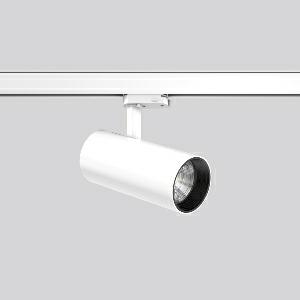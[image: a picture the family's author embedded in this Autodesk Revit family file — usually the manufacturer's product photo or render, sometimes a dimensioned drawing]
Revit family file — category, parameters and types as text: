
# Revit family: deecos_s_mini_742208_002_3_ff77
name_source: partatom
category: Lighting Fixtures
units: mm (PartAtom-declared; Revit-internal decimal feet)

## family parameters
Cut with Voids When Loaded = No
Host = Face
Light Source = No
Part Type = Normal
Room Calculation Point = No
Round Connector Dimension = Use Diameter
Shared = No

## types (1)
- DEECOS S mini (1 x LED Modul 935, 2900 lm, 3500)
    Apparent Load = 29 VA
    Approval mark = CE
    CIE Flux Codes = 98 100 100 100 100
    Color Rendering = 92
    Color Temperature = 3500
    Default Elevation = 1800 mm
    Description = Series: DEECOS S mini
LED surface-mounted projector in modern design with no visible cooling ribs. Housing: die-cast aluminium, powder-coated. Rotation range: 356°. Swivel range: 90°. Black plastic ring and recessed LED to prevent glare from the side. Optical assembly with lens made of plastic (polycarbonate) for the best homogeneous light distribution - can be changed without tools. Best colour rendering index Ra>90. With multi adaptor for 3-circuit tracks 230 V. Suitable for Track on ceiling, Wall track. High quality converter without flickering and stroboscopic effect. The following accessories can be mounted without use of tools: interchangeable lenses, decorative glasses, honeycomb louvre, clear and frosted diffusers, white interchangeable plastic ring. 
Colour: traffic white, matt (RAL 9016)
Diameter: 87 mm
Height: 214 mm
Lamp: LED
Socket: without socket
Colour temperature: 3500K
Colour rendering index (CRI): 92
System power: 29 W
Rated luminous flux: 2900 lm
Luminous efficiency: 100 lm/W
Control gear: Regulated power supply
Protection class: I
Type of protection: IP 20
    Height = 214 mm
    Lamp = 1 x LED Modul 935
    Lamp Light Flux = 2900 lm
    Lamp count = 1
    Length = 87 mm
    Lifetime = 50000 h
    Luminous efficacy = 100 lm/W
    Manufacturer = RZB
    ModVariant = No
    Model = 742208.002.3
    Mounting Place = Ceiling
    Mounting Type = Rail mounted
    Number of Poles = 1
    OnlyDefault = Yes
    Power Factor = 1
    Product Name = DEECOS S mini
    Product group = Track mounted projectors
    ProductGroupID = 301
    Protection Class = Protection class I
    Protection Degree = IP 20
    RLX_Detail_Level = 1
    RLX_Emergency_Light_Flux = 0 lm
    RLX_Emergency_Type = 0
    RLX_Emergency_Type_DB = No
    RlxData = <blob elided: 35461 chars, md5=12b38ac5>
    Socket = socket
    Standby Power = 0 W
    System Light Flux = 2900 lm
    System Power = 29 W
    Type Comments = Product without accessories
    Type Image = 741930.002.jpg
    URL = http://relux.com
    VarID = ---
    Voltage = 230 V
    Voltage Range = 220-240 V
    Weight = 0.00 kg
    Width = 0 mm  [stored 0 ft]

note: [stored X ft] marks values corroborated as IEEE doubles in the binary element streams (Revit-internal decimal feet)

## geometry (parser evidence)
native form markers: Blend x4, Sweep x11
no freeform markers — native parametric forms only
